# Revit family: Sink-Pedestal-Lavatory-KOHLER-Memoirs-K-2239T_1
name_source: partatom
category: Plumbing Fixtures
revit_build: Autodesk Revit 2017 (Build: 20160225_1515(x64)
units: mm (PartAtom-declared; Revit-internal decimal feet)

## family parameters
Cut with Voids When Loaded = No
Host = Face
OmniClass Number = 23.31.13.00
OmniClass Title = Sinks
Part Type = Normal
Room Calculation Point = No
Round Connector Dimension = Use Diameter
Shared = No

## types (6) — shared parameters
ADA Compliant = No
Assembly Code = D2010400
CW Connection = No
Cold Water Inlet = Cold Water Inlet
Date Modified = 08/13/2020
Default Elevation = 36"
Drain Included = No
HW Connection = No
Height = 8"
Hot Water Inlet = Hot Water Inlet
Length = 19 7/8"
Manufacturer = KOHLER Co.
Master Format 2014 = 22 41 16
Master Format 2014 Name = Residential Lavatories and Sinks
Material = Fireclay
Product Name = Memoirs
URL = http://www.kohler.com.cn
Vent Connection = No
Waste Connection = Yes
Waste Water Outlet = Waste Water Outlet
WaterSense Certified = No
Width = 24 3/16"

## per-type parameters (varying)
| type | 4 Inch Faucet Hole | 8 Inch Faucet Hole | Description | Faucet Hole Spacing | Finish | Model | Single Faucet Hole | Type |
| Single Faucet Hole, 0-White | No | No | Pedestal Lavatory with single faucet holes | 0" | KOHLER-Fireclay-0-White | K-2239T-1-0 | Yes | 1 |
| Single Faucet Hole, 47-Almond | No | No | Pedestal Lavatory with single faucet holes | 0" | KOHLER-Fireclay-47-Almond | K-2239T-1-47 | Yes | 2 |
| Single Faucet Hole, 96-Biscuit | No | No | Pedestal Lavatory with single faucet holes | 0" | KOHLER-Fireclay-96-Biscuit | K-2239T-1-96 | Yes | 3 |
| 4 Inch Faucet Hole, 0-White | Yes | No | Pedestal Lavatory with 4 inch widespread faucet holes | 4" | KOHLER-Fireclay-0-White | K-2239T-4-0 | No | 4 |
| 8 Inch Faucet Hole, 0-White | No | Yes | Pedestal Lavatory with 8 inch widespread faucet holes | 8" | KOHLER-Fireclay-0-White | K-2239T-8-0 | No | 5 |
| 8 Inch Faucet Hole, 96-Biscuit | No | Yes | Pedestal Lavatory with 8 inch widespread faucet holes | 8" | KOHLER-Fireclay-96-Biscuit | K-2239T-8-96 | No | 6 |

## geometry (parser evidence)
native form markers: Sweep x5
no freeform markers — native parametric forms only
